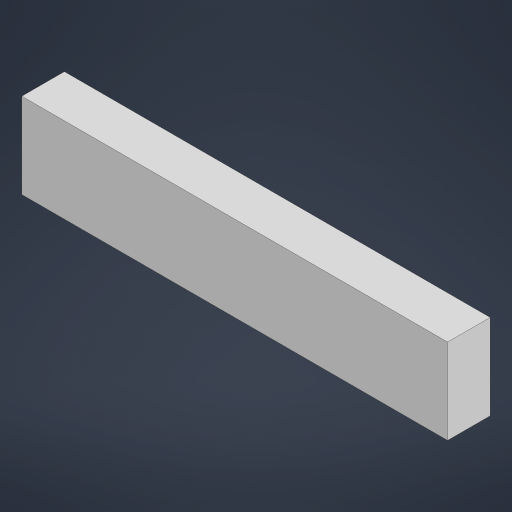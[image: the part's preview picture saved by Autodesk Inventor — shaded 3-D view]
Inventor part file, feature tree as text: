
AUTODESK INVENTOR PART (.ipt)
format: ipt  version: 2024 (Build 280153000, 153)  size: 151,040 bytes
history: native  units: in
note: dims shown in document units (in); Inventor stores cm internally (conversion verified against a paired STEP export)
features: extrude x1, sketch x1
ambient origin geometry x8: Origin, YZ Plane, XZ Plane, XY Plane, X Axis, Y Axis, Z Axis, Center Point
bodies: Solid1 (feature_tree)
feature tree (2):
  extrude  "Extrusion1"  Depth=0.7874in
  sketch  "Sketch1"  dims[d0=3.937in d1=0.7874in d2=0.3937in d3=0.0in]
